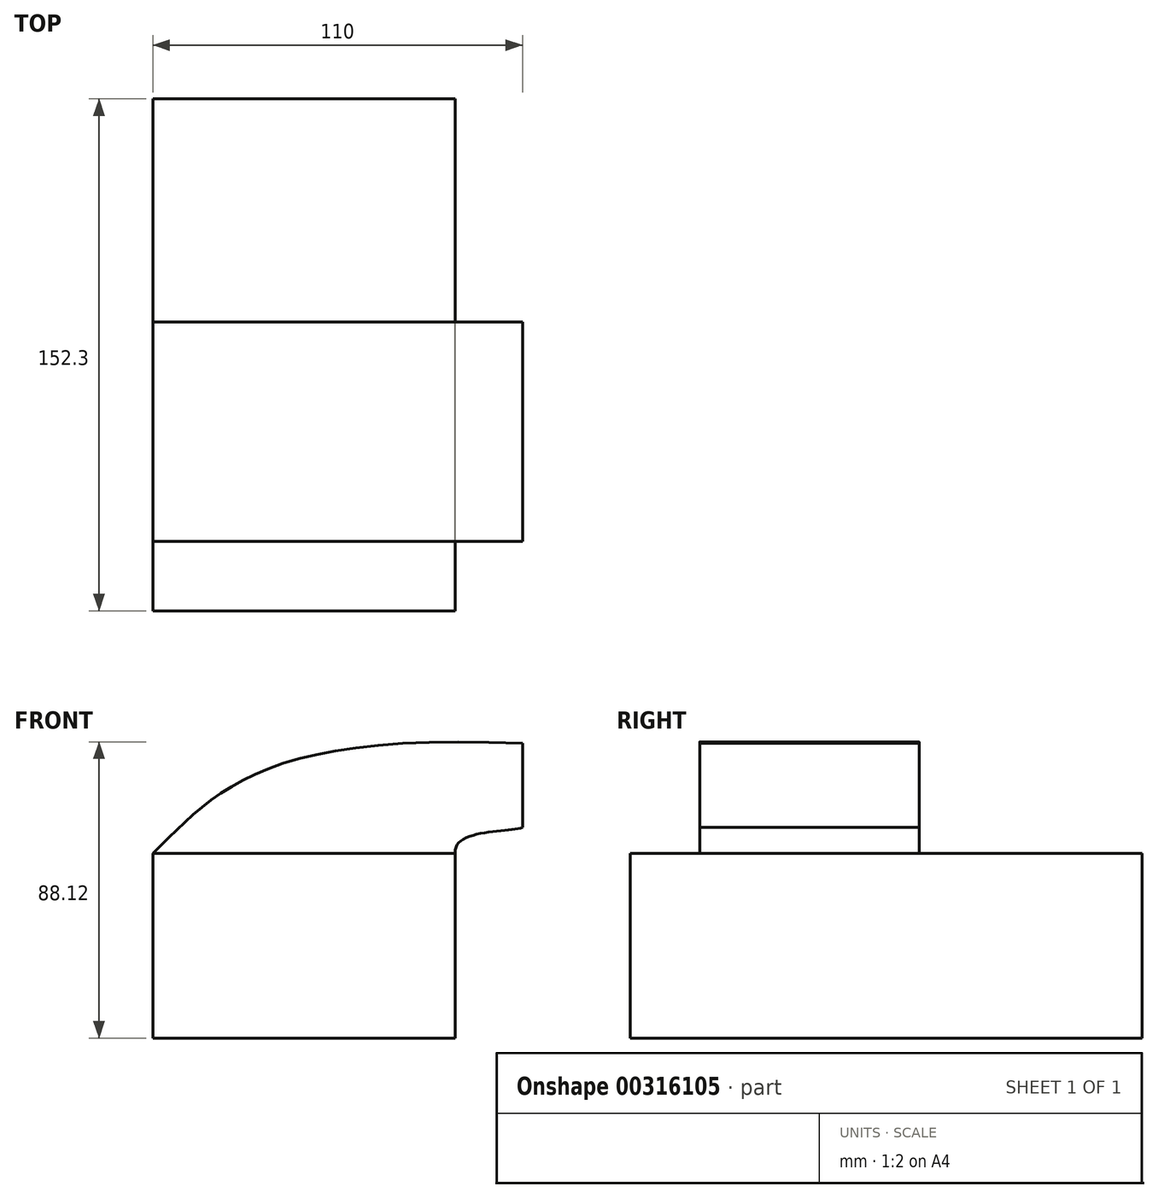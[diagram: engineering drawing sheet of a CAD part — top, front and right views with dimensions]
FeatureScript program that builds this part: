
annotation { "Feature Type Name" : "Feature", "Feature Type Description" : "" }
export const myFeature = defineFeature(function(context is Context, id is Id, definition is map)
    precondition{}
    {
        {
            var Q0;
            Q0=qCreatedBy(makeId("Front.planeOp"),FACE);
            var sketch = newSketch(context, id + "F0", { "sketchPlane" : qUnion([Q0])});
            skLineSegment(sketch, "E0.bottom", {"start": v(-43.92, 24.58) * mm, "end": v(46.08, 24.58) * mm});
            skLineSegment(sketch, "E0.top", {"start": v(-43.92, -30.42) * mm, "end": v(46.08, -30.42) * mm});
            skLineSegment(sketch, "E0.left", {"start": v(-43.92, 24.58) * mm, "end": v(-43.92, -30.42) * mm});
            skLineSegment(sketch, "E0.right", {"start": v(46.08, 24.58) * mm, "end": v(46.08, -30.42) * mm});
            skLineSegment(sketch, "E1.bottom", {"start": v(66.08, 57.26) * mm, "end": v(101.08, 57.26) * mm});
            skLineSegment(sketch, "E1.top", {"start": v(66.08, 32.26) * mm, "end": v(101.08, 32.26) * mm});
            skLineSegment(sketch, "E1.left", {"start": v(66.08, 57.26) * mm, "end": v(66.08, 32.26) * mm});
            skLineSegment(sketch, "E1.right", {"start": v(101.08, 57.26) * mm, "end": v(101.08, 32.26) * mm});
            skFitSpline(sketch, "E2", {"points": [v(-43.92, 24.58) * mm, v(66.08, 57.26) * mm], "startDerivative": vector(56.38, 53.25) * mm, "endDerivative": vector(237.83, -10.59) * mm});
            skFitSpline(sketch, "E3", {"points": [v(46.08, 24.58) * mm, v(66.08, 32.26) * mm], "startDerivative": vector(-2.04, 22.06) * mm, "endDerivative": vector(13.13, 5.09) * mm});
            skLineSegment(sketch, "E4.bottom", {"start": v(66.08, 57.26) * mm, "end": v(112.71, 57.26) * mm});
            skLineSegment(sketch, "E4.top", {"start": v(66.08, 70.09) * mm, "end": v(112.71, 70.09) * mm});
            skLineSegment(sketch, "E4.left", {"start": v(66.08, 57.26) * mm, "end": v(66.08, 70.09) * mm});
            skLineSegment(sketch, "E4.right", {"start": v(112.71, 57.26) * mm, "end": v(112.71, 70.09) * mm});
            skSolve(sketch);
        }
        {
            var Q0;
            Q0=makeQuery(id+"F0.imprint","IMPRINT",FACE,{"disambiguationData":[TD([[makeQuery(id+"F0.imprint","IMPRINT",EDGE,{"derivedFrom":sQuery(id+"F0.wireOp",EDGE,"E0.bottom")}),-1.0]])]});
            extrude(context, id + "F1", {"entities" : qUnion([Q0]), "depth" : 86 * mm});
        }
        {
            var Q0;
            Q0=makeQuery(id+"F0.imprint","IMPRINT",FACE,{"disambiguationData":[TD([[makeQuery(id+"F0.imprint","IMPRINT",EDGE,{"derivedFrom":sQuery(id+"F0.wireOp",EDGE,"E0.bottom")}),-1.0]])]});
            extrude(context, id + "F2", {"entities" : qUnion([Q0]), "operationType" : NewBodyOperationType.ADD, "endBound" : BoundingType.SYMMETRIC, "depth" : 25 * mm});
        }
        {
            var Q0;
            Q0=makeQuery(id+"F2.opExtrude","CAP_FACE",FACE,{"disambiguationData":[OSD([sQuery(id+"F0.wireOp",EDGE,"E0.bottom"),sQuery(id+"F0.wireOp",EDGE,"E0.top"),sQuery(id+"F0.wireOp",EDGE,"E0.left"),sQuery(id+"F0.wireOp",EDGE,"E0.right")])],"isStart":true});
            extrude(context, id + "F3", {"entities" : qUnion([Q0]), "operationType" : NewBodyOperationType.ADD, "depth" : 53.8 * mm});
        }
        {
            var Q0;
            Q0=makeQuery(id+"F0.imprint","IMPRINT",FACE,{"disambiguationData":[TD([[makeQuery(id+"F0.imprint","IMPRINT",EDGE,{"derivedFrom":sQuery(id+"F0.wireOp",EDGE,"E0.bottom")}),1.0]])]});
            extrude(context, id + "F4", {"entities" : qUnion([Q0]), "operationType" : NewBodyOperationType.ADD, "depth" : 65.3 * mm});
        }
    });
